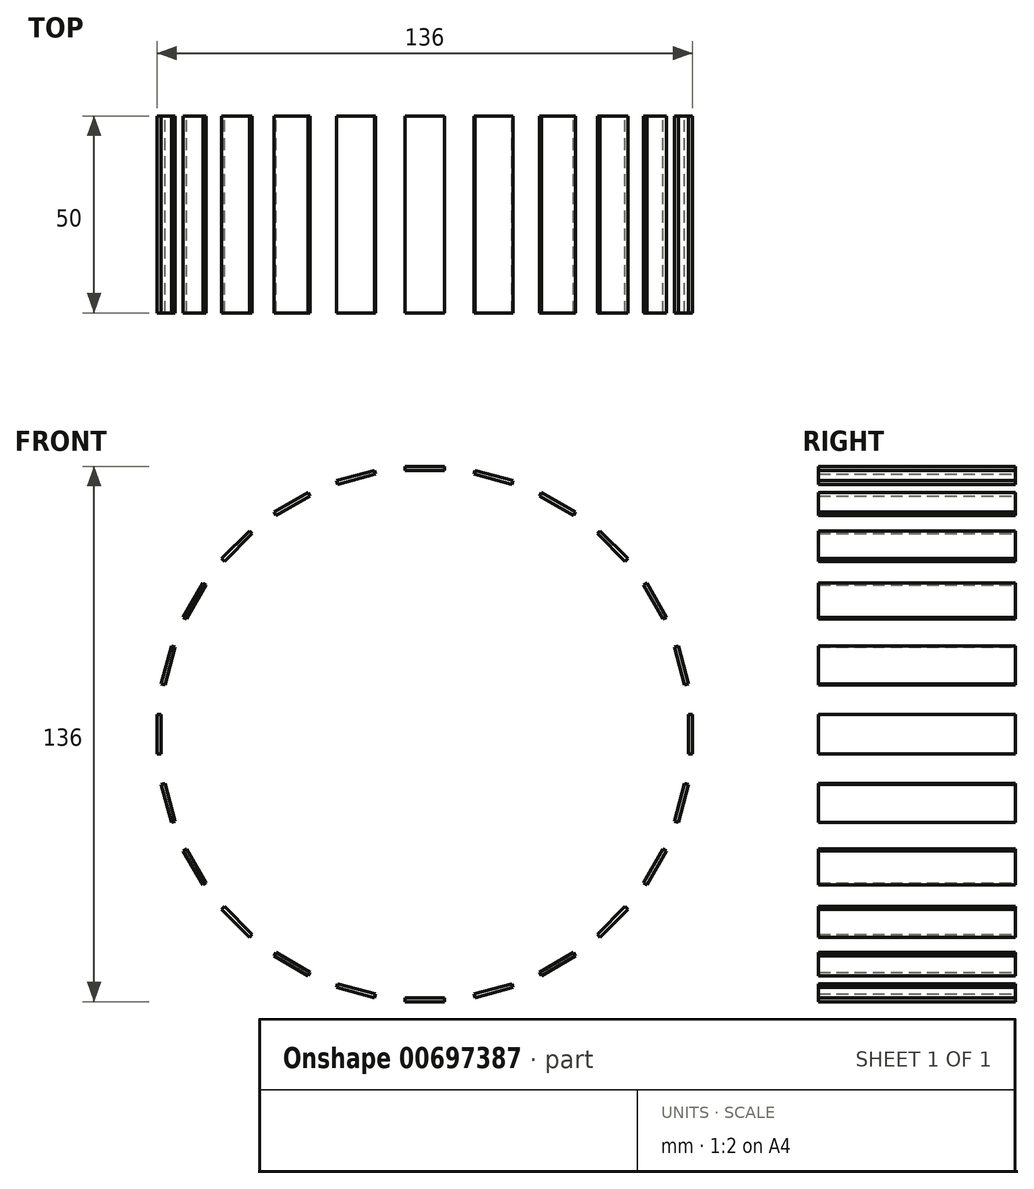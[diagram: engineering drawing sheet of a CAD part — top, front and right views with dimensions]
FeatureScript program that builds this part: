
annotation { "Feature Type Name" : "Feature", "Feature Type Description" : "" }
export const myFeature = defineFeature(function(context is Context, id is Id, definition is map)
    precondition{}
    {
        {
            var Q0;
            Q0=qCreatedBy(makeId("Front.planeOp"),FACE);
            var sketch = newSketch(context, id + "F0", { "sketchPlane" : qUnion([Q0])});
            skLineSegment(sketch, "E0", {"start": v(0, 67) * mm, "end": v(5, 67) * mm});
            skLineSegment(sketch, "E1", {"start": v(5, 68) * mm, "end": v(-5, 68) * mm});
            skLineSegment(sketch, "E2", {"start": v(-5, 68) * mm, "end": v(-5, 67) * mm});
            skLineSegment(sketch, "E3", {"start": v(-5, 67) * mm, "end": v(0, 67) * mm});
            skLineSegment(sketch, "E4", {"start": v(5, 67) * mm, "end": v(5, 68) * mm});
            skCircle(sketch, "E5", {"center": v(0, 0) * mm, "radius": 5 * mm});
            skLineSegment(sketch, "E6", {"start": v(-0.76, 4.94) * mm, "end": v(0.76, 4.94) * mm});
            skSolve(sketch);
        }
        {
            var Q0;
            Q0=makeQuery(id+"F0.imprint","IMPRINT",FACE,{"disambiguationData":[TD([[makeQuery(id+"F0.imprint","IMPRINT",EDGE,{"derivedFrom":sQuery(id+"F0.wireOp",EDGE,"E5")}),1.0]])]});
            var Q1;
            Q1=makeQuery(id+"F0.imprint","IMPRINT",FACE,{"disambiguationData":[TD([[makeQuery(id+"F0.imprint","IMPRINT",EDGE,{"derivedFrom":sQuery(id+"F0.wireOp",EDGE,"E0")}),1.0]])]});
            extrude(context, id + "F1", {"entities" : qUnion([Q0, Q1]), "depth" : 50 * mm, "offsetDistance" : 25 * mm});
        }
        {
            var Q0;
            Q0=makeQuery(id+"F1.opExtrude","SWEPT_BODY",BODY,{"disambiguationData":[OSD([sQuery(id+"F0.wireOp",EDGE,"E0"),sQuery(id+"F0.wireOp",EDGE,"E1"),sQuery(id+"F0.wireOp",EDGE,"E2"),sQuery(id+"F0.wireOp",EDGE,"E3"),sQuery(id+"F0.wireOp",EDGE,"E4")])]});
            var Q1;
            Q1=makeQuery(id+"F1.opExtrude","SWEPT_FACE",FACE,{"disambiguationData":[OSD([sQuery(id+"F0.wireOp",EDGE,"E5")])]});
            circularPattern(context, id + "F2", {"entities" : qUnion([Q0]), "axis" : qUnion([Q1]), "angle" : 360 * degree, "instanceCount" : 24, "equalSpace" : true});
        }
        {
            var Q0;
            Q0=makeQuery(id+"F1.opExtrude","CAP_FACE",FACE,{"disambiguationData":[OSD([sQuery(id+"F0.wireOp",EDGE,"E5")])],"isStart":false});
            extrude(context, id + "F3", {"entities" : qUnion([Q0]), "operationType" : NewBodyOperationType.REMOVE, "oppositeDirection" : true, "depth" : 50 * mm, "offsetDistance" : 25 * mm});
        }
    });
